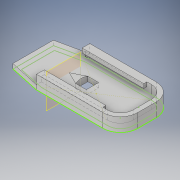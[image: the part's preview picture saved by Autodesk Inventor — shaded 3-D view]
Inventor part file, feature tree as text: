
AUTODESK INVENTOR PART (.ipt)
format: ipt  version: 2017 (Build 210142000, 142)  size: 172,544 bytes
history: native  units: in
note: dims shown in document units (in); Inventor stores cm internally (conversion verified against a paired STEP export)
features: sketch x6, extrude x5, plane x1, loft x1
ambient origin geometry x8: Origin, YZ Plane, XZ Plane, XY Plane, X Axis, Y Axis, Z Axis, Center Point
bodies: Solid1 (feature_tree)
feature tree (13):
  sketch  "Sketch1"  dims[d11=0.1181in d12=0.0in d13=0.3445in d14=0.0in]
  extrude  "Extrusion1"  Depth=0.3445in TaperAngle=0.0deg
  extrude  "Extrusion2"  Depth=0.2264in TaperAngle=0.0deg
  extrude  "Extrusion3"  Depth=0.0787in
  extrude  "Extrusion4"  Depth=1.5748in TaperAngle=0.0deg
  extrude  "Extrusion5"  Depth=0.315in
  sketch  "Sketch5"  dims[d25=0.2756in d26=0.315in]
  plane  "Work Plane2"
  loft  "Loft1"
  sketch  "Sketch2"  dims[d15=0.2264in d16=3.937in d17=0.0in]
  sketch  "Sketch3"  dims[d18=0.1181in d19=0.0787in]
  sketch  "Sketch4"  dims[d20=0.0787in d21=1.5748in d22=0.0in]
  sketch  "Sketch6"  dims[d27=1.2992in d28=0.0in d30=0.0in d31=90.0deg d32=0.0in d33=90.0deg]
